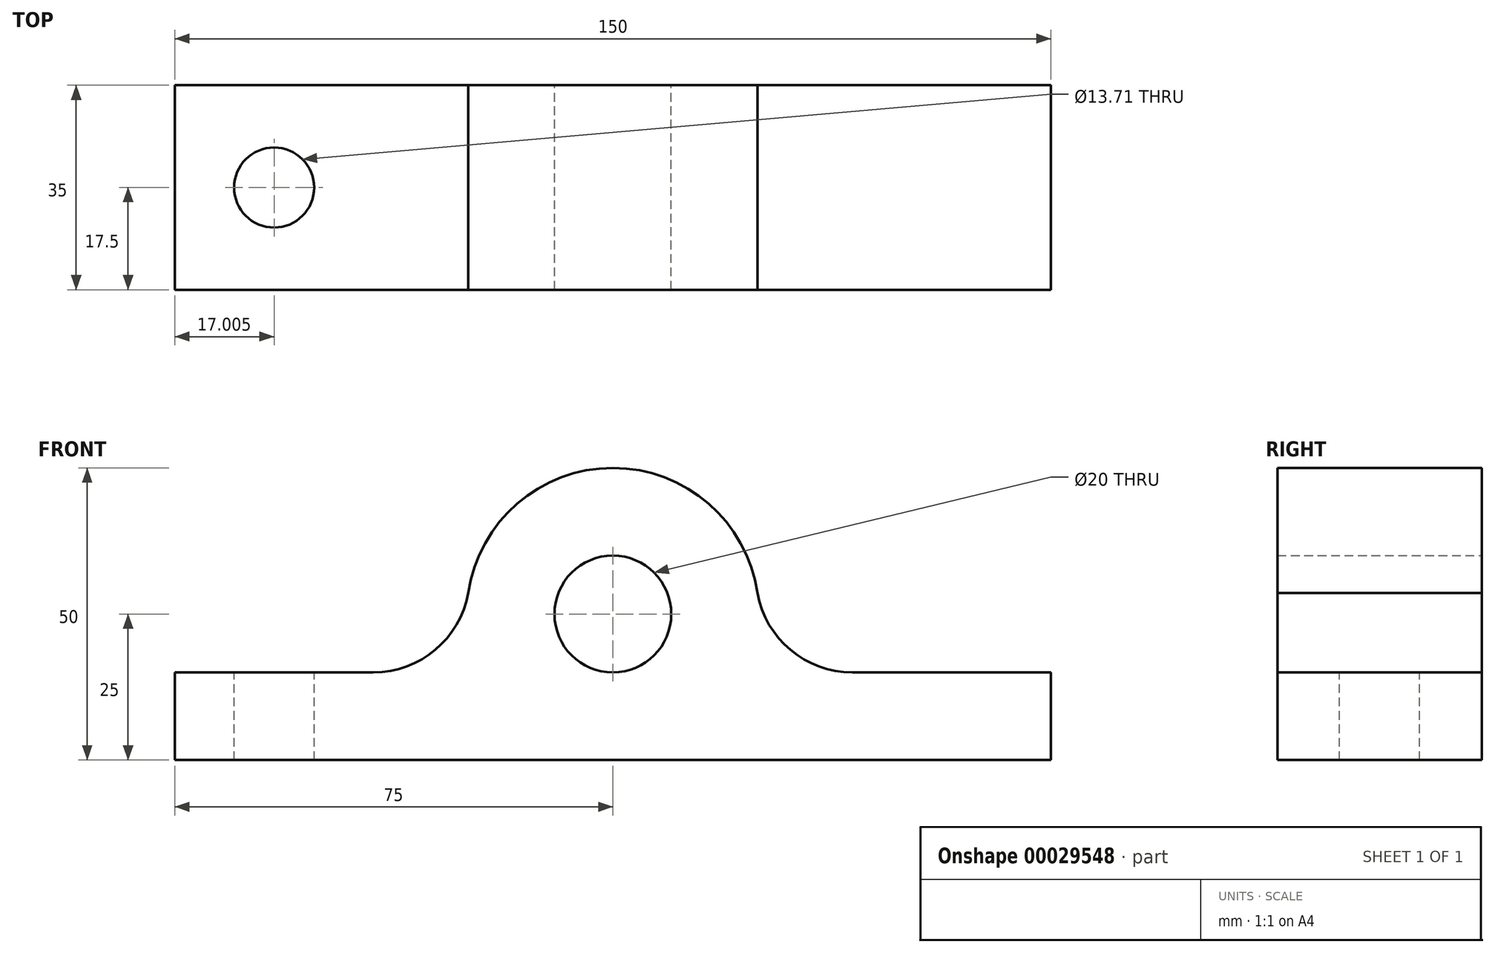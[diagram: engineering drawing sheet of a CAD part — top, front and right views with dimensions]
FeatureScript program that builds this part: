
annotation { "Feature Type Name" : "Feature", "Feature Type Description" : "" }
export const myFeature = defineFeature(function(context is Context, id is Id, definition is map)
    precondition{}
    {
        {
            var Q0;
            Q0=qCreatedBy(makeId("Front.planeOp"),FACE);
            var sketch = newSketch(context, id + "F0", { "sketchPlane" : qUnion([Q0])});
            skLineSegment(sketch, "E0", {"start": v(0, 0) * mm, "end": v(-75, 0) * mm});
            skLineSegment(sketch, "E1", {"start": v(-75, 0) * mm, "end": v(-75, 15) * mm});
            skLineSegment(sketch, "E2", {"start": v(0, 0) * mm, "end": v(75, 0) * mm});
            skLineSegment(sketch, "E3", {"start": v(75, 0) * mm, "end": v(75, 15) * mm});
            skLineSegment(sketch, "E4", {"start": v(-75, 15) * mm, "end": v(-41, 15) * mm});
            skArc(sketch, "E5", {"start": v(24.74, 28.59) * mm, "mid": v(0, 50) * mm, "end": v(-24.74, 28.59) * mm});
            skArc(sketch, "E6", {"start": v(24.62, 29.32) * mm, "mid": v(30.17, 19.06) * mm, "end": v(41.1, 15) * mm});
            skPoint(sketch, "E6.first.point", {"position": v(24.74, 28.59) * mm});
            skPoint(sketch, "E6.second.point", {"position": v(41.1, 15) * mm});
            skPoint(sketch, "E6.third.point", {"position": v(55.2, 22.95) * mm});
            skArc(sketch, "E7.MirrorC", {"start": v(-24.62, 29.32) * mm, "mid": v(-30.17, 19.06) * mm, "end": v(-41.1, 15) * mm});
            skCircle(sketch, "E8", {"center": v(0, 25) * mm, "radius": 10 * mm});
            skLineSegment(sketch, "E9.trimOffspring", {"start": v(41, 15) * mm, "end": v(75, 15) * mm});
            skSolve(sketch);
        }
        {
            var Q0;
            Q0 = qSketchRegion(id + "F0", true);
            extrude(context, id + "F1", {"entities" : qUnion([Q0]), "depth" : 35 * mm});
        }
        {
            var Q0;
            Q0=makeQuery(id+"F1.opExtrude","SWEPT_FACE",FACE,{"disambiguationData":[OSD([sQuery(id+"F0.wireOp",EDGE,"E4")])]});
            var sketch = newSketch(context, id + "F2", { "sketchPlane" : qUnion([Q0])});
            skCircle(sketch, "E10", {"center": v(-58, -17.5) * mm, "radius": 6.85 * mm});
            skCircle(sketch, "E11.MirrorC", {"center": v(58, -17.5) * mm, "radius": 6.85 * mm});
            skSolve(sketch);
        }
        {
            var Q0;
            Q0=makeQuery(id+"F2.imprint","IMPRINT",FACE,{"disambiguationData":[TD([[makeQuery(id+"F2.imprint","IMPRINT",EDGE,{"derivedFrom":sQuery(id+"F2.wireOp",EDGE,"E11.MirrorC")}),-1.0]])]});
            var Q1;
            Q1=makeQuery(id+"F2.imprint","IMPRINT",FACE,{"disambiguationData":[TD([[makeQuery(id+"F2.imprint","IMPRINT",EDGE,{"derivedFrom":sQuery(id+"F2.wireOp",EDGE,"E10")}),1.0]])]});
            var Q2;
            Q2=sQuery(id+"F2.wireOp",EDGE,"E10");
            var Q3;
            Q3=sQuery(id+"F2.wireOp",EDGE,"E11.MirrorC");
            extrude(context, id + "F3", {"entities" : qUnion([Q0, Q1]), "operationType" : NewBodyOperationType.REMOVE, "surfaceEntities" : qUnion([Q2, Q3]), "oppositeDirection" : true, "depth" : 15 * mm});
        }
    });
